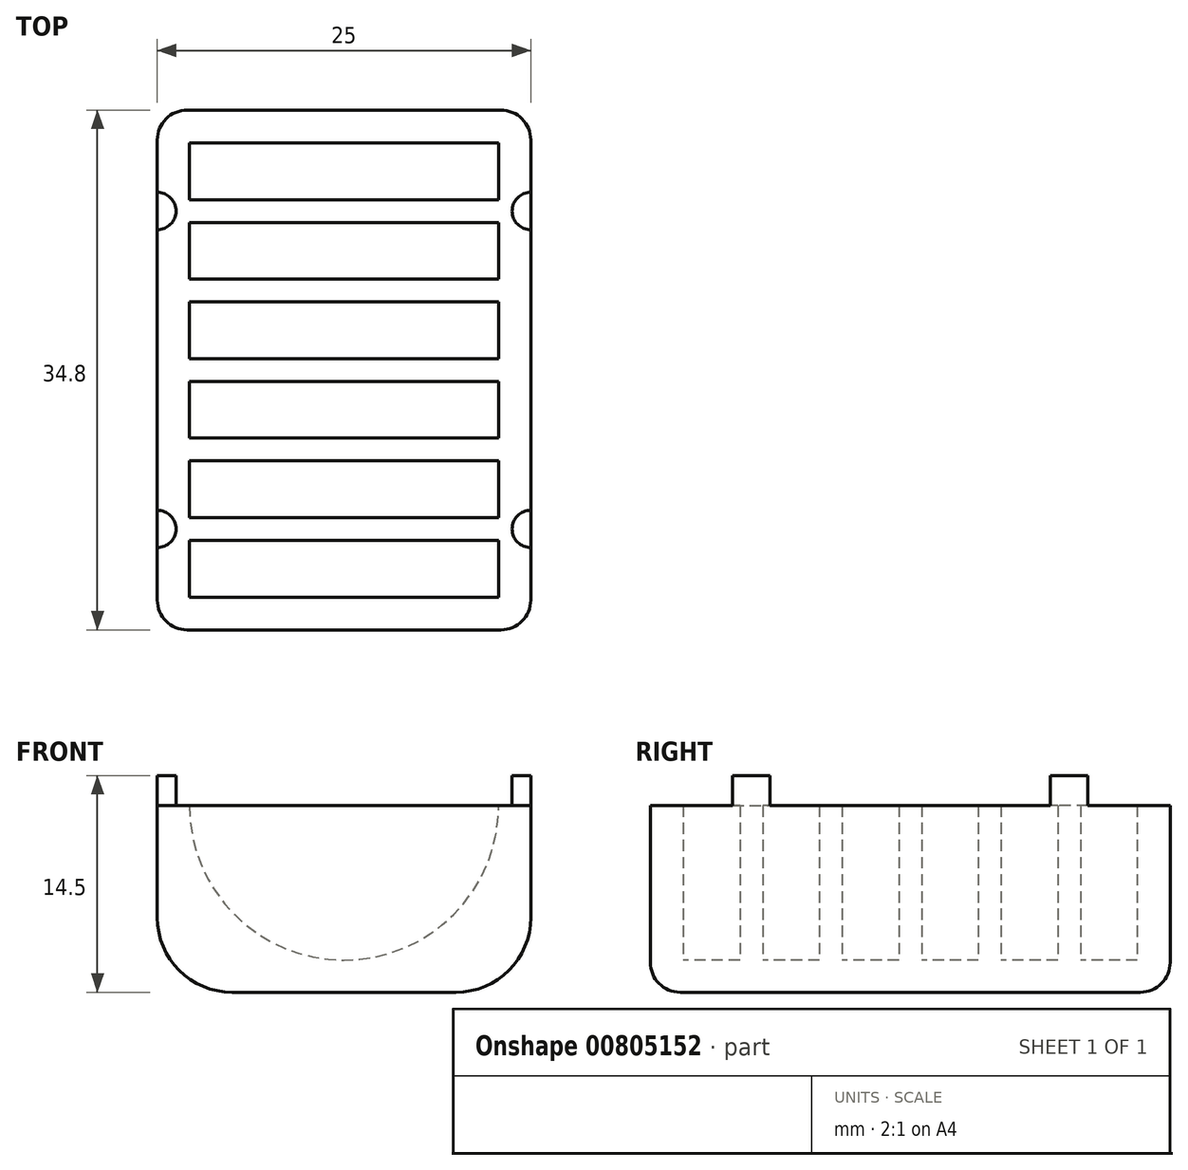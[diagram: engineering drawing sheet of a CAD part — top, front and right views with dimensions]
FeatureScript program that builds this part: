
annotation { "Feature Type Name" : "Feature", "Feature Type Description" : "" }
export const myFeature = defineFeature(function(context is Context, id is Id, definition is map)
    precondition{}
    {
        {
            var Q0;
            Q0=qCreatedBy(makeId("Top.planeOp"),FACE);
            var sketch = newSketch(context, id + "F0", { "sketchPlane" : qUnion([Q0])});
            skLineSegment(sketch, "E0.bottom", {"start": v(-30.1, 7.68) * mm, "end": v(-5.1, 7.68) * mm});
            skLineSegment(sketch, "E0.top", {"start": v(-30.1, -27.12) * mm, "end": v(-5.1, -27.12) * mm});
            skLineSegment(sketch, "E0.left", {"start": v(-30.1, 7.68) * mm, "end": v(-30.1, -27.12) * mm});
            skLineSegment(sketch, "E0.right", {"start": v(-5.1, 7.68) * mm, "end": v(-5.1, -27.12) * mm});
            skSolve(sketch);
        }
        {
            var Q0;
            Q0=qSketchRegion(id+"F0",true);
            extrude(context, id + "F1", {"entities" : qUnion([Q0]), "depth" : (25 / 2) * mm, "offsetDistance" : 25 * mm});
        }
        {
            var Q0;
            Q0=makeQuery(id+"F1.opExtrude","SWEPT_FACE",FACE,{"disambiguationData":[OSD([sQuery(id+"F0.wireOp",EDGE,"E0.top")])]});
            var sketch = newSketch(context, id + "F2", { "sketchPlane" : qUnion([Q0])});
            skCircle(sketch, "E1", {"center": v(-17.6, 12.5) * mm, "radius": 10.35 * mm});
            skSolve(sketch);
        }
        {
            var Q0;
            Q0=qSketchRegion(id+"F2",true);
            extrude(context, id + "F3", {"entities" : qUnion([Q0]), "operationType" : NewBodyOperationType.REMOVE, "oppositeDirection" : true, "depth" : (34.8 - 2.2) * mm, "offsetDistance" : 25 * mm, "hasSecondDirection" : true, "secondDirectionOppositeDirection" : true, "secondDirectionDepth" : (2.2) * mm});
        }
        {
            var Q0;
            Q0=makeQuery(id+"F1.opExtrude","CAP_FACE",FACE,{"disambiguationData":[OSD([sQuery(id+"F0.wireOp",EDGE,"E0.bottom"),sQuery(id+"F0.wireOp",EDGE,"E0.top"),sQuery(id+"F0.wireOp",EDGE,"E0.left"),sQuery(id+"F0.wireOp",EDGE,"E0.right")])],"isStart":false});
            var sketch = newSketch(context, id + "F4", { "sketchPlane" : qUnion([Q0])});
            skLineSegment(sketch, "E2.bottom", {"start": v(-27.95, 1.68) * mm, "end": v(-7.25, 1.68) * mm});
            skLineSegment(sketch, "E2.top", {"start": v(-27.95, 0.16) * mm, "end": v(-7.25, 0.16) * mm});
            skLineSegment(sketch, "E2.left", {"start": v(-27.95, 1.68) * mm, "end": v(-27.95, 0.16) * mm});
            skLineSegment(sketch, "E2.right", {"start": v(-7.25, 1.68) * mm, "end": v(-7.25, 0.16) * mm});
            skLineSegment(sketch, "E3.bottom", {"start": v(-27.95, -3.64) * mm, "end": v(-7.25, -3.64) * mm});
            skLineSegment(sketch, "E3.top", {"start": v(-27.95, -5.16) * mm, "end": v(-7.25, -5.16) * mm});
            skLineSegment(sketch, "E3.left", {"start": v(-27.95, -3.64) * mm, "end": v(-27.95, -5.16) * mm});
            skLineSegment(sketch, "E3.right", {"start": v(-7.25, -3.64) * mm, "end": v(-7.25, -5.16) * mm});
            skLineSegment(sketch, "E4.bottom", {"start": v(-27.95, -8.96) * mm, "end": v(-7.25, -8.96) * mm});
            skLineSegment(sketch, "E4.top", {"start": v(-27.95, -10.48) * mm, "end": v(-7.25, -10.48) * mm});
            skLineSegment(sketch, "E4.left", {"start": v(-27.95, -8.96) * mm, "end": v(-27.95, -10.48) * mm});
            skLineSegment(sketch, "E4.right", {"start": v(-7.25, -8.96) * mm, "end": v(-7.25, -10.48) * mm});
            skLineSegment(sketch, "E5.bottom", {"start": v(-27.95, -14.28) * mm, "end": v(-7.25, -14.28) * mm});
            skLineSegment(sketch, "E5.top", {"start": v(-27.95, -15.8) * mm, "end": v(-7.25, -15.8) * mm});
            skLineSegment(sketch, "E5.left", {"start": v(-27.95, -14.28) * mm, "end": v(-27.95, -15.8) * mm});
            skLineSegment(sketch, "E5.right", {"start": v(-7.25, -14.28) * mm, "end": v(-7.25, -15.8) * mm});
            skLineSegment(sketch, "E6.top", {"start": v(-27.95, -21.12) * mm, "end": v(-7.25, -21.12) * mm});
            skLineSegment(sketch, "E7", {"start": v(-27.95, -21.12) * mm, "end": v(-27.95, -19.6) * mm});
            skLineSegment(sketch, "E8", {"start": v(-27.95, -19.6) * mm, "end": v(-7.25, -19.6) * mm});
            skLineSegment(sketch, "E9", {"start": v(-7.25, -19.6) * mm, "end": v(-7.25, -21.12) * mm});
            skSolve(sketch);
        }
        {
            var Q0;
            Q0=qSketchRegion(id+"F4",true);
            extrude(context, id + "F5", {"entities" : qUnion([Q0]), "operationType" : NewBodyOperationType.ADD, "oppositeDirection" : true, "depth" : 10.6 * mm, "offsetDistance" : 25 * mm});
        }
        {
            var Q0;
            Q0=makeQuery(id+"F1.opExtrude","CAP_EDGE",EDGE,{"disambiguationData":[OSD([sQuery(id+"F0.wireOp",EDGE,"E0.right")])],"isStart":true});
            var Q1;
            Q1=makeQuery(id+"F1.opExtrude","CAP_EDGE",EDGE,{"disambiguationData":[OSD([sQuery(id+"F0.wireOp",EDGE,"E0.left")])],"isStart":true});
            fillet(context, id + "F6", {"entities" : qUnion([Q0, Q1]), "radius" : 5 * mm, "tangentPropagation" : true, "allowEdgeOverflow" : false});
        }
        {
            var Q0;
            Q0=makeQuery(id+"F1.opExtrude","SWEPT_EDGE",EDGE,{"disambiguationData":[OSD([sQuery(id+"F0.wireOp",EDGE,"E0.top"),sQuery(id+"F0.wireOp",EDGE,"E0.right")])]});
            var Q1;
            Q1=makeQuery(id+"F1.opExtrude","SWEPT_EDGE",EDGE,{"disambiguationData":[OSD([sQuery(id+"F0.wireOp",EDGE,"E0.bottom"),sQuery(id+"F0.wireOp",EDGE,"E0.right")])]});
            fillet(context, id + "F7", {"entities" : qUnion([Q0, Q1]), "radius" : 2 * mm, "tangentPropagation" : true, "allowEdgeOverflow" : false});
        }
        {
            var Q0;
            Q0=makeQuery(id+"F5.boolean.opBoolean","MERGE",FACE,{"derivedFrom":[makeQuery(id+"F1.opExtrude","CAP_FACE",FACE,{"disambiguationData":[OSD([sQuery(id+"F0.wireOp",EDGE,"E0.bottom"),sQuery(id+"F0.wireOp",EDGE,"E0.top"),sQuery(id+"F0.wireOp",EDGE,"E0.left"),sQuery(id+"F0.wireOp",EDGE,"E0.right")])],"isStart":false}),makeQuery(id+"F5.opExtrude","CAP_FACE",FACE,{"disambiguationData":[OSD([sQuery(id+"F4.wireOp",EDGE,"E2.bottom"),sQuery(id+"F4.wireOp",EDGE,"E2.top"),sQuery(id+"F4.wireOp",EDGE,"E2.left"),sQuery(id+"F4.wireOp",EDGE,"E2.right")])],"isStart":true}),makeQuery(id+"F5.opExtrude","CAP_FACE",FACE,{"disambiguationData":[OSD([sQuery(id+"F4.wireOp",EDGE,"E3.bottom"),sQuery(id+"F4.wireOp",EDGE,"E3.top"),sQuery(id+"F4.wireOp",EDGE,"E3.left"),sQuery(id+"F4.wireOp",EDGE,"E3.right")])],"isStart":true}),makeQuery(id+"F5.opExtrude","CAP_FACE",FACE,{"disambiguationData":[OSD([sQuery(id+"F4.wireOp",EDGE,"E4.bottom"),sQuery(id+"F4.wireOp",EDGE,"E4.top"),sQuery(id+"F4.wireOp",EDGE,"E4.left"),sQuery(id+"F4.wireOp",EDGE,"E4.right")])],"isStart":true}),makeQuery(id+"F5.opExtrude","CAP_FACE",FACE,{"disambiguationData":[OSD([sQuery(id+"F4.wireOp",EDGE,"E5.bottom"),sQuery(id+"F4.wireOp",EDGE,"E5.top"),sQuery(id+"F4.wireOp",EDGE,"E5.left"),sQuery(id+"F4.wireOp",EDGE,"E5.right")])],"isStart":true}),makeQuery(id+"F5.opExtrude","CAP_FACE",FACE,{"disambiguationData":[OSD([sQuery(id+"F4.wireOp",EDGE,"E6.top"),sQuery(id+"F4.wireOp",EDGE,"E7"),sQuery(id+"F4.wireOp",EDGE,"E8"),sQuery(id+"F4.wireOp",EDGE,"E9")])],"isStart":true})]});
            var sketch = newSketch(context, id + "F8", { "sketchPlane" : qUnion([Q0])});
            skArc(sketch, "E10", {"start": v(-30.1, -0.33) * mm, "mid": v(-28.85, 0.92) * mm, "end": v(-30.1, 2.17) * mm});
            skArc(sketch, "E11.1.0.0", {"start": v(-5.1, 2.17) * mm, "mid": v(-6.35, 0.92) * mm, "end": v(-5.1, -0.33) * mm});
            skArc(sketch, "E12.MirrorC", {"start": v(-5.1, -21.6) * mm, "mid": v(-6.35, -20.36) * mm, "end": v(-5.1, -19.1) * mm});
            skArc(sketch, "E13.MirrorC", {"start": v(-30.1, -19.1) * mm, "mid": v(-28.85, -20.36) * mm, "end": v(-30.1, -21.6) * mm});
            skLineSegment(sketch, "E14", {"start": v(-30.1, -19.1) * mm, "end": v(-30.1, -21.6) * mm});
            skLineSegment(sketch, "E15", {"start": v(-5.1, -19.1) * mm, "end": v(-5.1, -21.6) * mm});
            skLineSegment(sketch, "E16", {"start": v(-5.1, 2.17) * mm, "end": v(-5.1, -0.33) * mm});
            skLineSegment(sketch, "E17", {"start": v(-30.1, 2.17) * mm, "end": v(-30.1, -0.33) * mm});
            skSolve(sketch);
        }
        {
            var Q0;
            Q0=qSketchRegion(id+"F8",true);
            extrude(context, id + "F9", {"entities" : qUnion([Q0]), "operationType" : NewBodyOperationType.ADD, "depth" : 2 * mm, "offsetDistance" : 25 * mm});
        }
    });
